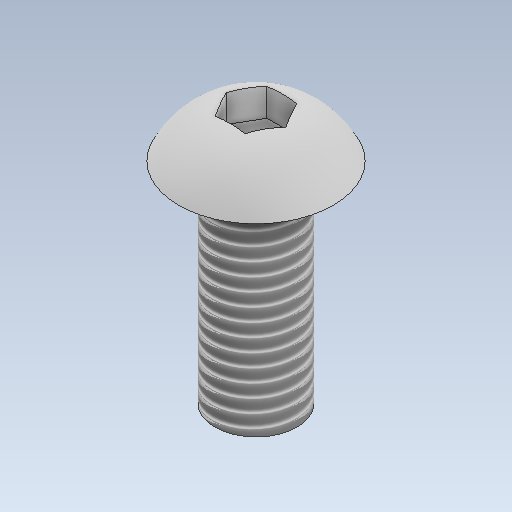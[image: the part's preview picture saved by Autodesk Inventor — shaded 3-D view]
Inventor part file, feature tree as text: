
AUTODESK INVENTOR PART (.ipt)
format: ipt  version: 2023 (Build 270158000, 158)  size: 163,840 bytes
history: native  units: in
note: dims shown in document units (in); Inventor stores cm internally (conversion verified against a paired STEP export)
features: sketch x3, extrude x2, revolve x1, thread x1, plane x1
ambient origin geometry x8: Origin, YZ Plane, XZ Plane, XY Plane, X Axis, Y Axis, Z Axis, Center Point
bodies: Solid1 (feature_tree)
feature tree (8):
  revolve  "Revolution1"  [1 undecoded]
  extrude  "Extrusion1"  Depth=0.1969in
  thread  "Thread1"  [1 undecoded]
  plane  "Work Plane1"
  extrude  "Extrusion2"  [1 undecoded]
  sketch  "Sketch1"  dims[d0=0.185in d1=0.1181in]
  sketch  "Sketch2"  dims[d2=90.0deg d3=0.1969in d4=0.5039in d5=0.0in]
  sketch  "Sketch3"  dims[d6=0.5039in d7=0.0in d8=-0.1181in d9=0.062in d10=0.0787in d11=0.0in]
note: 3 required parameter values undecoded (feature->parameter linkage not recoverable at this tier; creation-order binding heuristic only, values carry confidence <= 0.55)